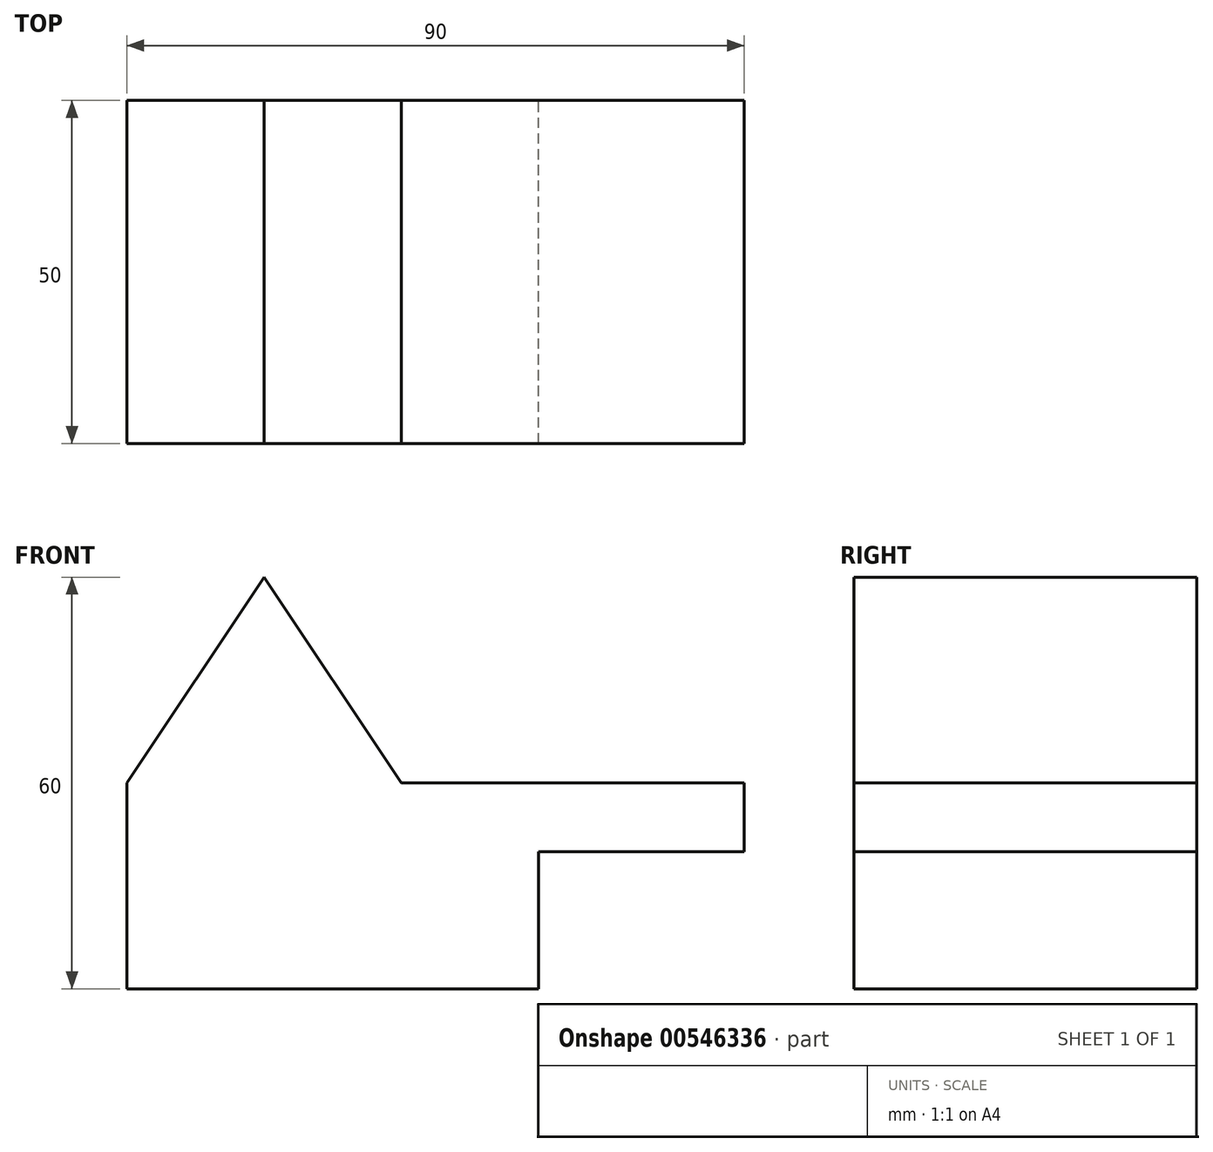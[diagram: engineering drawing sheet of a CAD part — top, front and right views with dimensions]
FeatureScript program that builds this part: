
annotation { "Feature Type Name" : "Feature", "Feature Type Description" : "" }
export const myFeature = defineFeature(function(context is Context, id is Id, definition is map)
    precondition{}
    {
        {
            var Q0;
            Q0=qCreatedBy(makeId("Front.planeOp"),FACE);
            var sketch = newSketch(context, id + "F0", { "sketchPlane" : qUnion([Q0])});
            skLineSegment(sketch, "E0.bottom", {"start": v(45, -30) * mm, "end": v(-45, -30) * mm});
            skLineSegment(sketch, "E0.top", {"start": v(45, 30) * mm, "end": v(-45, 30) * mm});
            skLineSegment(sketch, "E0.left", {"start": v(45, -30) * mm, "end": v(45, 30) * mm});
            skLineSegment(sketch, "E0.right", {"start": v(-45, -30) * mm, "end": v(-45, 30) * mm});
            skPoint(sketch, "E0.middle", {"position": v(0, 0) * mm});
            skSolve(sketch);
        }
        {
            var Q0;
            Q0 = qSketchRegion(id + "F0", true);
            extrude(context, id + "F1", {"entities" : qUnion([Q0]), "depth" : 50 * mm, "offsetDistance" : 25 * mm});
        }
        {
            var Q0;
            Q0=makeQuery(id+"F1.opExtrude","SWEPT_FACE",FACE,{"disambiguationData":[OSD([sQuery(id+"F0.wireOp",EDGE,"E0.bottom")])]});
            var sketch = newSketch(context, id + "F2", { "sketchPlane" : qUnion([Q0])});
            skLineSegment(sketch, "E1", {"start": v(15, 50) * mm, "end": v(15, 0) * mm});
            skSolve(sketch);
        }
        {
            var Q0;
            {var subQ0=sQuery(id+"F2.wireOp",EDGE,"E1");Q0=makeQuery(id+"F2.imprint","IMPRINT",FACE,{"disambiguationData":[TD([[makeQuery(id+"F2.imprint","IMPRINT",EDGE,{"derivedFrom":subQ0}),1.0]])]});}
            extrude(context, id + "F3", {"entities" : qUnion([Q0]), "operationType" : NewBodyOperationType.REMOVE, "oppositeDirection" : true, "depth" : 20 * mm, "offsetDistance" : 25 * mm});
        }
        {
            var Q0;
            Q0=makeQuery(id+"F1.opExtrude","CAP_FACE",FACE,{"disambiguationData":[OSD([sQuery(id+"F0.wireOp",EDGE,"E0.bottom"),sQuery(id+"F0.wireOp",EDGE,"E0.top"),sQuery(id+"F0.wireOp",EDGE,"E0.left"),sQuery(id+"F0.wireOp",EDGE,"E0.right")])],"isStart":true});
            var sketch = newSketch(context, id + "F4", { "sketchPlane" : qUnion([Q0])});
            skLineSegment(sketch, "E2", {"start": v(-45, 0) * mm, "end": v(5, 0) * mm});
            skLineSegment(sketch, "E3", {"start": v(45, 30) * mm, "end": v(25, 30) * mm, "construction": true});
            skLineSegment(sketch, "E4", {"start": v(25, 30) * mm, "end": v(45, 0) * mm});
            skLineSegment(sketch, "E5", {"start": v(25, 30) * mm, "end": v(5, 0) * mm});
            skSolve(sketch);
        }
        {
            var Q0;
            {var subQ0=sQuery(id+"F4.wireOp",EDGE,"E4");Q0=makeQuery(id+"F4.imprint","IMPRINT",FACE,{"disambiguationData":[TD([[makeQuery(id+"F4.imprint","IMPRINT",EDGE,{"derivedFrom":subQ0}),1.0]])]});}
            extrude(context, id + "F5", {"entities" : qUnion([Q0]), "operationType" : NewBodyOperationType.REMOVE, "endBound" : BoundingType.THROUGH_ALL, "oppositeDirection" : true, "depth" : 25 * mm, "offsetDistance" : 25 * mm});
        }
        {
            var Q0;
            {var subQ0=sQuery(id+"F4.wireOp",EDGE,"E2");Q0=makeQuery(id+"F4.imprint","IMPRINT",FACE,{"disambiguationData":[TD([[makeQuery(id+"F4.imprint","IMPRINT",EDGE,{"derivedFrom":subQ0}),1.0]])]});}
            extrude(context, id + "F6", {"entities" : qUnion([Q0]), "operationType" : NewBodyOperationType.REMOVE, "endBound" : BoundingType.THROUGH_ALL, "oppositeDirection" : true, "depth" : 25 * mm, "offsetDistance" : 25 * mm});
        }
    });
